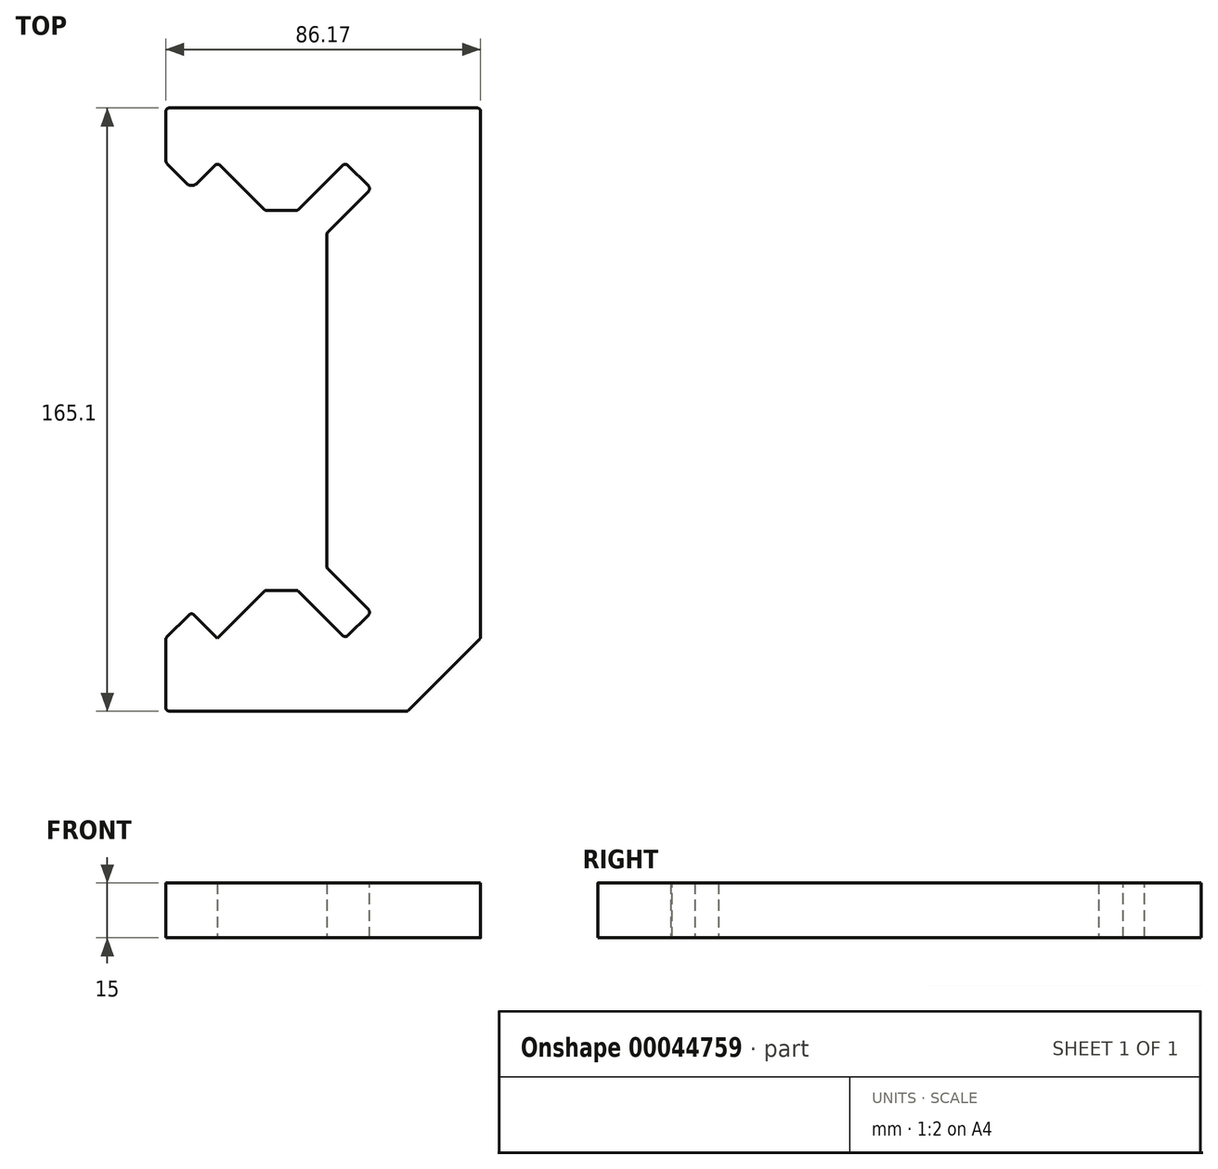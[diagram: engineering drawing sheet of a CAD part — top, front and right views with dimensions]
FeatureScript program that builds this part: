
annotation { "Feature Type Name" : "Feature", "Feature Type Description" : "" }
export const myFeature = defineFeature(function(context is Context, id is Id, definition is map)
    precondition{}
    {
        {
            var Q0;
            Q0=qCreatedBy(makeId("Top.planeOp"),FACE);
            var sketch = newSketch(context, id + "F0", { "sketchPlane" : qUnion([Q0])});
            skLineSegment(sketch, "E0", {"start": v(-40.61, 73.97) * mm, "end": v(45.56, 73.97) * mm});
            skLineSegment(sketch, "E1", {"start": v(45.56, 73.97) * mm, "end": v(45.56, -71.13) * mm});
            skLineSegment(sketch, "E2", {"start": v(-40.61, 73.97) * mm, "end": v(-40.61, 58.97) * mm});
            skLineSegment(sketch, "E3", {"start": v(-33.54, 51.9) * mm, "end": v(-40.61, 58.97) * mm});
            skLineSegment(sketch, "E4", {"start": v(-33.54, 51.9) * mm, "end": v(-26.47, 58.97) * mm});
            skLineSegment(sketch, "E5", {"start": v(-26.47, 58.97) * mm, "end": v(-13.42, 45.92) * mm});
            skLineSegment(sketch, "E6", {"start": v(-13.42, 45.92) * mm, "end": v(-4.56, 45.92) * mm});
            skLineSegment(sketch, "E7", {"start": v(-4.56, 45.92) * mm, "end": v(8.49, 58.97) * mm});
            skLineSegment(sketch, "E8", {"start": v(8.49, 58.97) * mm, "end": v(15.56, 51.9) * mm});
            skLineSegment(sketch, "E9", {"start": v(15.56, 51.9) * mm, "end": v(3.5, 39.85) * mm});
            skLineSegment(sketch, "E10", {"start": v(3.5, 39.85) * mm, "end": v(3.5, -52) * mm});
            skLineSegment(sketch, "E11", {"start": v(3.5, -52) * mm, "end": v(15.56, -64.06) * mm});
            skLineSegment(sketch, "E12", {"start": v(15.56, -64.06) * mm, "end": v(8.49, -71.13) * mm});
            skLineSegment(sketch, "E13", {"start": v(8.49, -71.13) * mm, "end": v(-4.56, -58.08) * mm});
            skLineSegment(sketch, "E14", {"start": v(-4.56, -58.08) * mm, "end": v(-13.42, -58.08) * mm});
            skLineSegment(sketch, "E15", {"start": v(-40.61, -91.13) * mm, "end": v(25.56, -91.13) * mm});
            skLineSegment(sketch, "E16", {"start": v(-9, 43.92) * mm, "end": v(-18.5, 34.42) * mm, "construction": true});
            skLineSegment(sketch, "E17", {"start": v(-18.5, 34.42) * mm, "end": v(-18.5, -46.58) * mm, "construction": true});
            skLineSegment(sketch, "E18", {"start": v(-18.5, -46.58) * mm, "end": v(-9, -56.08) * mm, "construction": true});
            skLineSegment(sketch, "E19", {"start": v(-9, -56.08) * mm, "end": v(0.5, -46.58) * mm, "construction": true});
            skLineSegment(sketch, "E20", {"start": v(0.5, 34.42) * mm, "end": v(-9, 43.92) * mm, "construction": true});
            skLineSegment(sketch, "E21", {"start": v(0.5, 34.42) * mm, "end": v(0.5, -46.58) * mm, "construction": true});
            skPoint(sketch, "E22", {"position": v(12.02, -67.6) * mm});
            skLineSegment(sketch, "E23", {"start": v(12.02, -67.6) * mm, "end": v(-4.24, -51.33) * mm, "construction": true});
            skPoint(sketch, "E24", {"position": v(-30, 55.44) * mm});
            skPoint(sketch, "E25", {"position": v(-13.74, 39.17) * mm});
            skLineSegment(sketch, "E26", {"start": v(-30, 55.44) * mm, "end": v(-13.74, 39.17) * mm, "construction": true});
            skLineSegment(sketch, "E27", {"start": v(-4.24, 39.17) * mm, "end": v(12.02, 55.44) * mm, "construction": true});
            skLineSegment(sketch, "E28", {"start": v(0, 50.49) * mm, "end": v(7.07, 43.41) * mm, "construction": true});
            skLineSegment(sketch, "E29", {"start": v(-40.61, -71.13) * mm, "end": v(-40.61, -91.13) * mm});
            skLineSegment(sketch, "E30", {"start": v(7.07, -55.57) * mm, "end": v(0, -62.64) * mm, "construction": true});
            skPoint(sketch, "E31", {"position": v(3.54, -59.1) * mm});
            skLineSegment(sketch, "E32", {"start": v(45.56, -71.13) * mm, "end": v(25.56, -91.13) * mm});
            skLineSegment(sketch, "E33", {"start": v(-17.99, 50.49) * mm, "end": v(-21.52, 46.95) * mm, "construction": true});
            skLineSegment(sketch, "E34", {"start": v(-13.42, -58.08) * mm, "end": v(-26.47, -71.13) * mm});
            skLineSegment(sketch, "E35", {"start": v(-26.47, -71.13) * mm, "end": v(-33.54, -64.06) * mm});
            skLineSegment(sketch, "E36", {"start": v(-18.7, -63.35) * mm, "end": v(-22.23, -59.81) * mm, "construction": true});
            skLineSegment(sketch, "E37", {"start": v(-13.74, -51.33) * mm, "end": v(-30, -67.6) * mm, "construction": true});
            skLineSegment(sketch, "E38", {"start": v(-33.54, -64.06) * mm, "end": v(-40.61, -71.13) * mm});
            skSolve(sketch);
        }
        {
            var Q0;
            Q0 = qSketchRegion(id + "F0", true);
            extrude(context, id + "F1", {"entities" : qUnion([Q0]), "depth" : 15 * mm});
        }
        {
            var Q0;
            Q0=makeQuery(id+"F1.opExtrude","SWEPT_EDGE",EDGE,{"disambiguationData":[OSD([sQuery(id+"F0.wireOp",EDGE,"E3"),sQuery(id+"F0.wireOp",EDGE,"E4")])]});
            var Q1;
            Q1=makeQuery(id+"F1.opExtrude","SWEPT_EDGE",EDGE,{"disambiguationData":[OSD([sQuery(id+"F0.wireOp",EDGE,"E2"),sQuery(id+"F0.wireOp",EDGE,"E3")])]});
            fillet(context, id + "F2", {"entities" : qUnion([Q0, Q1]), "radius" : 2 * mm, "tangentPropagation" : true, "allowEdgeOverflow" : false});
        }
        {
            var Q0;
            Q0=makeQuery(id+"F1.opExtrude","SWEPT_EDGE",EDGE,{"disambiguationData":[OSD([sQuery(id+"F0.wireOp",EDGE,"E4"),sQuery(id+"F0.wireOp",EDGE,"E5")])]});
            var Q1;
            Q1=makeQuery(id+"F1.opExtrude","SWEPT_EDGE",EDGE,{"disambiguationData":[OSD([sQuery(id+"F0.wireOp",EDGE,"E5"),sQuery(id+"F0.wireOp",EDGE,"E6")])]});
            var Q2;
            Q2=makeQuery(id+"F1.opExtrude","SWEPT_EDGE",EDGE,{"disambiguationData":[OSD([sQuery(id+"F0.wireOp",EDGE,"E6"),sQuery(id+"F0.wireOp",EDGE,"E7")])]});
            var Q3;
            Q3=makeQuery(id+"F1.opExtrude","SWEPT_EDGE",EDGE,{"disambiguationData":[OSD([sQuery(id+"F0.wireOp",EDGE,"E7"),sQuery(id+"F0.wireOp",EDGE,"E8")])]});
            var Q4;
            {var subQ0=sQuery(id+"F0.wireOp",EDGE,"E2");Q4=makeQuery(id+"F2.opFillet","BLEND_EDGE",EDGE,{"blendedFrom":[makeQuery(id+"F1.opExtrude","SWEPT_EDGE",EDGE,{"disambiguationData":[OSD([subQ0,sQuery(id+"F0.wireOp",EDGE,"E3")])]}),makeQuery(id+"F1.opExtrude","SWEPT_FACE",FACE,{"disambiguationData":[OSD([subQ0])]})],"blendedInto":[makeQuery(id+"F1.opExtrude","SWEPT_FACE",FACE,{"disambiguationData":[OSD([subQ0])]})]});}
            fillet(context, id + "F3", {"entities" : qUnion([Q0, Q1, Q2, Q3, Q4]), "radius" : 1 * mm, "tangentPropagation" : true, "allowEdgeOverflow" : false});
        }
        {
            var Q0;
            Q0=makeQuery(id+"F1.opExtrude","SWEPT_EDGE",EDGE,{"disambiguationData":[OSD([sQuery(id+"F0.wireOp",EDGE,"E29"),sQuery(id+"F0.wireOp",EDGE,"E38")])]});
            var Q1;
            Q1=makeQuery(id+"F1.opExtrude","SWEPT_EDGE",EDGE,{"disambiguationData":[OSD([sQuery(id+"F0.wireOp",EDGE,"E35"),sQuery(id+"F0.wireOp",EDGE,"E38")])]});
            var Q2;
            Q2=makeQuery(id+"F1.opExtrude","SWEPT_EDGE",EDGE,{"disambiguationData":[OSD([sQuery(id+"F0.wireOp",EDGE,"E14"),sQuery(id+"F0.wireOp",EDGE,"E34")])]});
            var Q3;
            Q3=makeQuery(id+"F1.opExtrude","SWEPT_EDGE",EDGE,{"disambiguationData":[OSD([sQuery(id+"F0.wireOp",EDGE,"E13"),sQuery(id+"F0.wireOp",EDGE,"E14")])]});
            var Q4;
            Q4=makeQuery(id+"F1.opExtrude","SWEPT_EDGE",EDGE,{"disambiguationData":[OSD([sQuery(id+"F0.wireOp",EDGE,"E11"),sQuery(id+"F0.wireOp",EDGE,"E12")])]});
            var Q5;
            Q5=makeQuery(id+"F1.opExtrude","SWEPT_EDGE",EDGE,{"disambiguationData":[OSD([sQuery(id+"F0.wireOp",EDGE,"E10"),sQuery(id+"F0.wireOp",EDGE,"E11")])]});
            var Q6;
            Q6=makeQuery(id+"F1.opExtrude","SWEPT_EDGE",EDGE,{"disambiguationData":[OSD([sQuery(id+"F0.wireOp",EDGE,"E9"),sQuery(id+"F0.wireOp",EDGE,"E10")])]});
            var Q7;
            Q7=makeQuery(id+"F1.opExtrude","SWEPT_EDGE",EDGE,{"disambiguationData":[OSD([sQuery(id+"F0.wireOp",EDGE,"E8"),sQuery(id+"F0.wireOp",EDGE,"E9")])]});
            fillet(context, id + "F4", {"entities" : qUnion([Q0, Q1, Q2, Q3, Q4, Q5, Q6, Q7]), "radius" : 1 * mm, "tangentPropagation" : true, "allowEdgeOverflow" : false});
        }
        {
            var Q0;
            Q0=makeQuery(id+"F1.opExtrude","SWEPT_EDGE",EDGE,{"disambiguationData":[OSD([sQuery(id+"F0.wireOp",EDGE,"E0"),sQuery(id+"F0.wireOp",EDGE,"E2")])]});
            var Q1;
            Q1=makeQuery(id+"F1.opExtrude","SWEPT_EDGE",EDGE,{"disambiguationData":[OSD([sQuery(id+"F0.wireOp",EDGE,"E12"),sQuery(id+"F0.wireOp",EDGE,"E13")])]});
            var Q2;
            Q2=makeQuery(id+"F1.opExtrude","SWEPT_EDGE",EDGE,{"disambiguationData":[OSD([sQuery(id+"F0.wireOp",EDGE,"E15"),sQuery(id+"F0.wireOp",EDGE,"E29")])]});
            var Q3;
            Q3=makeQuery(id+"F1.opExtrude","SWEPT_EDGE",EDGE,{"disambiguationData":[OSD([sQuery(id+"F0.wireOp",EDGE,"E0"),sQuery(id+"F0.wireOp",EDGE,"E1")])]});
            var Q4;
            Q4=makeQuery(id+"F1.opExtrude","SWEPT_EDGE",EDGE,{"disambiguationData":[OSD([sQuery(id+"F0.wireOp",EDGE,"E1"),sQuery(id+"F0.wireOp",EDGE,"E32")])]});
            var Q5;
            Q5=makeQuery(id+"F1.opExtrude","SWEPT_EDGE",EDGE,{"disambiguationData":[OSD([sQuery(id+"F0.wireOp",EDGE,"E15"),sQuery(id+"F0.wireOp",EDGE,"E32")])]});
            fillet(context, id + "F5", {"entities" : qUnion([Q0, Q1, Q2, Q3, Q4, Q5]), "radius" : 1 * mm, "tangentPropagation" : true, "allowEdgeOverflow" : false});
        }
    });
